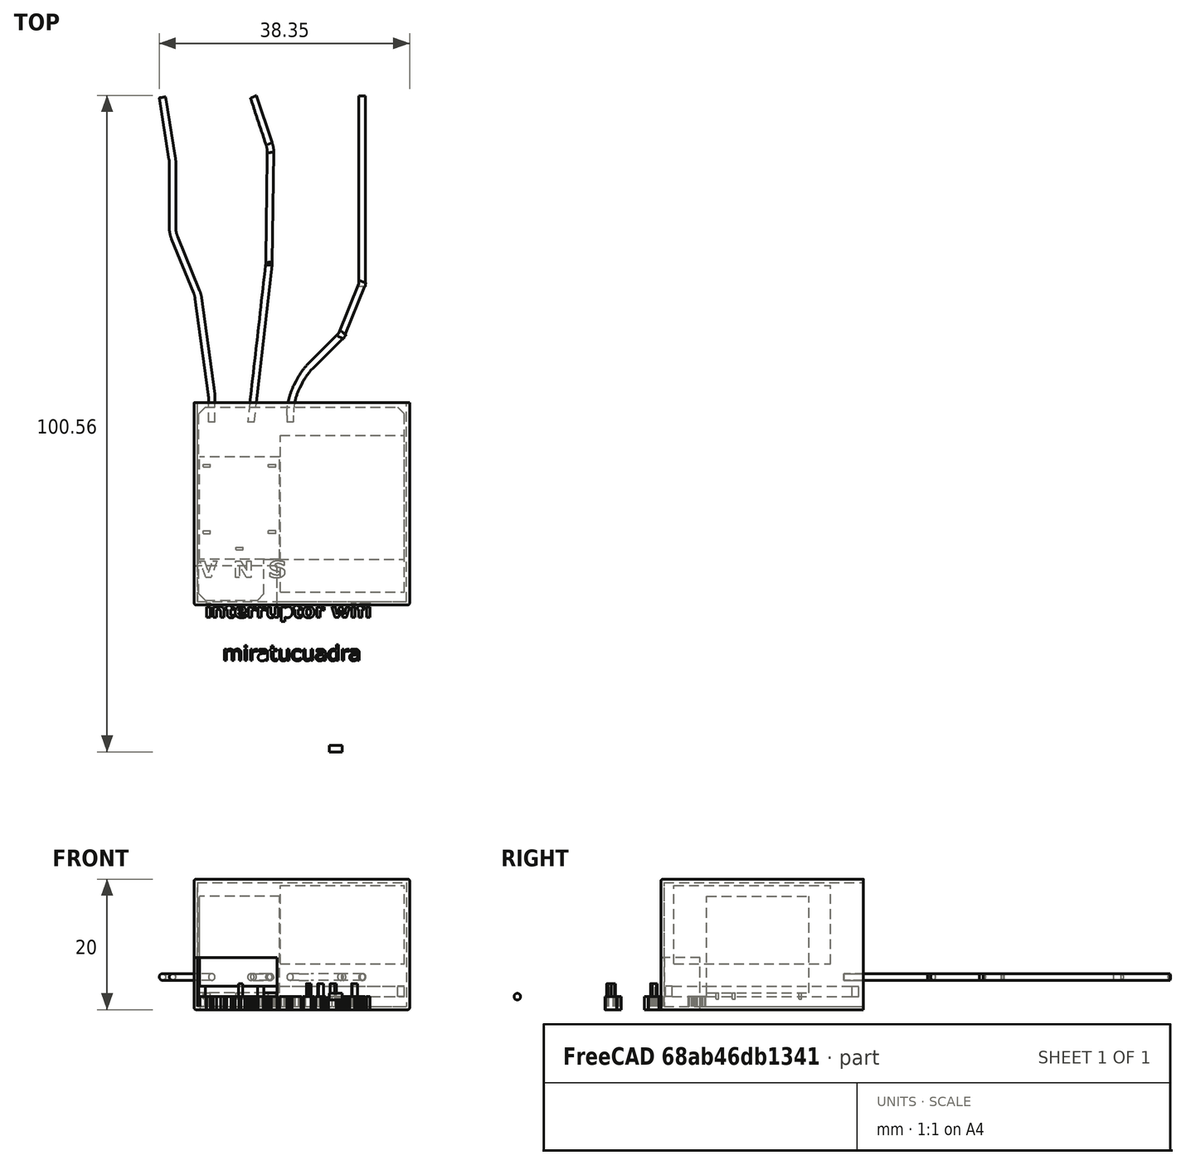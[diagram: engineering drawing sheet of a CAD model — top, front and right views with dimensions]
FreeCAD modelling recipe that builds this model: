
FCSTD DOCUMENT  (FreeCAD 0.20R29410 (Git))
Label: device01_funda_reprog
License: All rights reserved
LicenseURL: http://en.wikipedia.org/wiki/All_rights_reserved
objects: Part::Extrusion×42, Part::Feature×41, Part::Box×12, Part::Part2DObjectPython×6, Part::Cut×6, Part::MultiFuse×3, Part::Sweep×3, Part::Chamfer×2, Part::Fillet×1
note: 116 computed .brp shape members not serialized (recipe doc carries the construction recipe); baked Part::Feature solids carry a one-line shape summary decoded from their .brp

FEATURE [Part::Box] Box  label="fuente"
  AttacherType = Attacher::AttachEngine3D
  Height = 12
  Length = 19
  Placement = pos=(12.5,-5,5) rot=(0,0,1;0rad)
  Width = 24
FEATURE [Part::Box] Box002  label="placa"
  AttacherType = Attacher::AttachEngine3D
  Height = 1.6
  Length = 31.5
  Width = 23.3
FEATURE [Part::Box] Box003  label="placa2"
  AttacherType = Attacher::AttachEngine3D
  Height = 1.6
  Length = 10
  Placement = pos=(0,-6.3,0) rot=(0,0,1;0rad)
  Width = 6.3
FEATURE [Part::Chamfer] Chamfer
  Base = -> Box003
  Edges = 2 edges r=1: [Edge1,Edge5]
FEATURE [Part::Chamfer] Chamfer001
  Base = -> Box002
  Edges = 2 edges r=1: [Edge3,Edge7]
FEATURE [Part::MultiFuse] Fusion  label="plaqueta"
  Shapes = -> [Chamfer,Chamfer001]
FEATURE [Part::Box] Box004  label="cuerpo"
  AttacherType = Attacher::AttachEngine3D
  Height = 14.8
  Length = 15.7
  Placement = pos=(0,0,-1) rot=(0,0,1;0rad)
  Width = 12.3
FEATURE [Part::Box] Box005  label="pata002"
  AttacherType = Attacher::AttachEngine3D
  Height = 2.5
  Length = 0.4
  Placement = pos=(1.45,5.6,-2) rot=(0,0,1;0rad)
  Width = 1.1
FEATURE [Part::Box] Box006  label="pata003"
  AttacherType = Attacher::AttachEngine3D
  Height = 2.5
  Length = 0.4
  Placement = pos=(14.15,10.6,-2) rot=(0,0,1;0rad)
  Width = 1.1
FEATURE [Part::Box] Box007  label="pata004"
  AttacherType = Attacher::AttachEngine3D
  Height = 2.5
  Length = 0.4
  Placement = pos=(3.95,10.6,-2) rot=(0,0,1;0rad)
  Width = 1.1
FEATURE [Part::Box] Box008  label="pata005"
  AttacherType = Attacher::AttachEngine3D
  Height = 2.5
  Length = 0.4
  Placement = pos=(14.15,0.6,-2) rot=(0,0,1;0rad)
  Width = 1.1
FEATURE [Part::Box] Box009  label="pata1"
  AttacherType = Attacher::AttachEngine3D
  Height = 2.5
  Length = 0.4
  Placement = pos=(3.95,0.6,-2) rot=(0,0,1;0rad)
  Width = 1.1
FEATURE [Part::MultiFuse] Fusion001  label="relay"
  Placement = pos=(12.4,0,1.6) rot=(0,0,1;1.5708rad)
  Shapes = -> [Box009,Box007,Box005,Box006,Box008,Box004]
FEATURE [Part::Box] Box010  label="funda"
  AttacherType = Attacher::AttachEngine3D
  Height = 20
  Length = 33
  Placement = pos=(-0.7,-7,-2) rot=(0,0,1;0rad)
  Width = 31
FEATURE [Part::Part2DObjectPython] Circle  # Draft 2D object (typed FeaturePython)
  FirstAngle = 0
  LastAngle = 0
  MakeFace = true
  Placement = pos=(20,-17,0) rot=(0.57735,0.57735,0.57735;2.0944rad)
  Radius = 0.5
FEATURE [Part::Part2DObjectPython] DWire  # Draft 2D object (typed FeaturePython)
  ChamferSize = 0
  Closed = false
  End = (20,-11,0)
  FilletRadius = 4
  Length = 53.4054
  MakeFace = false
  Points = (6) [(-30,-1.83697e-15,0),(0,0,0),(10,-4,0),(16,-10,0),(18,-11,0),(20,-11,0)]
  Start = (-30,0,0)
  Subdivisions = 0
FEATURE [Part::Sweep] Sweep
  Frenet = false
  Sections = -> [Circle]
  Solid = true
  Spine = -> DWire
  Transition = 1
FEATURE [Part::Part2DObjectPython] DWire001  # Draft 2D object (typed FeaturePython)
  ChamferSize = 0
  Closed = false
  End = (-29.8507,-19.6083,0)
  FilletRadius = 4
  Length = 50.4185
  MakeFace = false
  Points = (4) [(20,-20,0),(-4.30719,-17.2304,0),(-22,-17,0),(-29.8507,-19.6083,0)]
  Start = (20,-20,0)
  Subdivisions = 0
FEATURE [Part::Part2DObjectPython] Circle001  # Draft 2D object (typed FeaturePython)
  FirstAngle = 0
  LastAngle = 0
  MakeFace = true
  Placement = pos=(20,-20,0) rot=(0.57735,0.57735,0.57735;2.0944rad)
  Radius = 0.5
FEATURE [Part::Sweep] Sweep001
  Frenet = false
  Placement = pos=(0,-3,0) rot=(0,0,1;0rad)
  Sections = -> [Circle001]
  Solid = true
  Spine = -> DWire001
  Transition = 1
FEATURE [Part::Part2DObjectPython] DWire002  # Draft 2D object (typed FeaturePython)
  ChamferSize = 0
  Closed = false
  End = (-29.774,-36.5606,0)
  FilletRadius = 4
  Length = 50.7764
  MakeFace = false
  Points = (6) [(20,-29,0),(16,-29,0),(0.525362,-31.1144,0),(-9,-35,0),(-20,-35,0),(-29.774,-36.5606,0)]
  Start = (20,-29,0)
  Subdivisions = 0
FEATURE [Part::Part2DObjectPython] Circle002  # Draft 2D object (typed FeaturePython)
  FirstAngle = 0
  LastAngle = 0
  MakeFace = true
  Placement = pos=(20,-29,0) rot=(0.57735,0.57735,0.57735;2.0944rad)
  Radius = 0.5
FEATURE [Part::Sweep] Sweep002
  Frenet = false
  Sections = -> [Circle002]
  Solid = true
  Spine = -> DWire002
  Transition = 1
FEATURE [Part::MultiFuse] Fusion002  label="cables"
  Placement = pos=(31,41,3) rot=(0,0,-1;1.5708rad)
  Shapes = -> [Sweep,Sweep001,Sweep002]
FEATURE [Part::Box] Box011  label="Cubo"
  AttacherType = Attacher::AttachEngine3D
  Height = 19
  Length = 32
  Placement = pos=(-0.2,-6.5,-1.5) rot=(0,0,1;0rad)
  Width = 35
FEATURE [Part::Cut] Cut  label="carcasa"
  Base = -> Box010
  Tool = -> Box011
FEATURE [Part::Fillet] Fillet  label="gabinete"
  Base = -> Cut
  Edges = 8 edges r=0.3: [Edge1,Edge2,Edge4,Edge5,Edge6,Edge7,Edge9,Edge16]
FEATURE [Part::Box] Box012  label="Cubo001"
  AttacherType = Attacher::AttachEngine3D
  Height = 10
  Length = 14
  Placement = pos=(-2,-11,-4) rot=(0,0,1;0rad)
  Width = 10
FEATURE [Part::Cut] Cut001
  Base = -> Fillet
  Tool = -> Box012
FEATURE [Part::Feature] path319
  shape: bbox 2.527 x 1.78 x 2e-07 mm, 0 faces, 0 solids (baked)
FEATURE [Part::Feature] path321
  shape: bbox 0.3287 x 0.3023 x 2e-07 mm, 0 faces, 0 solids (baked)
FEATURE [Part::Feature] path321001
  shape: bbox 0.2915 x 1.732 x 2e-07 mm, 0 faces, 0 solids (baked)
FEATURE [Part::Feature] path323
  shape: bbox 1.081 x 1.732 x 2e-07 mm, 0 faces, 0 solids (baked)
FEATURE [Part::Feature] path325
  shape: bbox 1.471 x 1.822 x 2e-07 mm, 0 faces, 0 solids (baked)
FEATURE [Part::Feature] path325001
  shape: bbox 0.8806 x 0.6852 x 2e-07 mm, 0 faces, 0 solids (baked)
FEATURE [Part::Feature] path327
  shape: bbox 1.09 x 2.263 x 2e-07 mm, 0 faces, 0 solids (baked)
FEATURE [Part::Feature] path329
  shape: bbox 1.448 x 1.78 x 2e-07 mm, 0 faces, 0 solids (baked)
FEATURE [Part::Feature] path331
  shape: bbox 1.405 x 1.811 x 2e-07 mm, 0 faces, 0 solids (baked)
FEATURE [Part::Feature] path333
  shape: bbox 1.448 x 1.78 x 2e-07 mm, 0 faces, 0 solids (baked)
FEATURE [Part::Feature] path335
  shape: bbox 1.471 x 1.822 x 2e-07 mm, 0 faces, 0 solids (baked)
FEATURE [Part::Feature] path335001
  shape: bbox 0.8806 x 0.6852 x 2e-07 mm, 0 faces, 0 solids (baked)
FEATURE [Part::Feature] path337
  shape: bbox 1.524 x 2.46 x 2e-07 mm, 0 faces, 0 solids (baked)
FEATURE [Part::Feature] path337001
  shape: bbox 0.9317 x 1.284 x 2e-07 mm, 0 faces, 0 solids (baked)
FEATURE [Part::Feature] path339
  shape: bbox 1.081 x 1.732 x 2e-07 mm, 0 faces, 0 solids (baked)
FEATURE [Part::Feature] path341
  shape: bbox 1.471 x 1.822 x 2e-07 mm, 0 faces, 0 solids (baked)
FEATURE [Part::Feature] path341001
  shape: bbox 0.8806 x 0.6852 x 2e-07 mm, 0 faces, 0 solids (baked)
FEATURE [Part::Feature] path357
  shape: bbox 2.643 x 2.596 x 2e-07 mm, 0 faces, 0 solids (baked)
FEATURE [Part::Feature] path354
  shape: bbox 2.361 x 2.596 x 2e-07 mm, 0 faces, 0 solids (baked)
FEATURE [Part::Feature] path351
  shape: bbox 2.22 x 2.69 x 2e-07 mm, 0 faces, 0 solids (baked)
FEATURE [Part::Feature] path288
  shape: bbox 0.5176 x 1.615 x 2e-07 mm, 0 faces, 0 solids (baked)
FEATURE [Part::Feature] path288001
  shape: bbox 0.5464 x 0.3925 x 2e-07 mm, 0 faces, 0 solids (baked)
FEATURE [Part::Feature] path290
  shape: bbox 1.622 x 1.659 x 2e-07 mm, 0 faces, 0 solids (baked)
FEATURE [Part::Feature] path292
  shape: bbox 1.215 x 2.108 x 2e-07 mm, 0 faces, 0 solids (baked)
FEATURE [Part::Feature] path294
  shape: bbox 1.708 x 1.708 x 2e-07 mm, 0 faces, 0 solids (baked)
FEATURE [Part::Feature] path294001
  shape: bbox 0.6715 x 0.3264 x 2e-07 mm, 0 faces, 0 solids (baked)
FEATURE [Part::Feature] path296
  shape: bbox 1.17 x 1.62 x 2e-07 mm, 0 faces, 0 solids (baked)
FEATURE [Part::Feature] path298
  shape: bbox 1.17 x 1.62 x 2e-07 mm, 0 faces, 0 solids (baked)
FEATURE [Part::Feature] path300
  shape: bbox 1.622 x 1.659 x 2e-07 mm, 0 faces, 0 solids (baked)
FEATURE [Part::Feature] path302
  shape: bbox 1.685 x 2.252 x 2e-07 mm, 0 faces, 0 solids (baked)
FEATURE [Part::Feature] path302001
  shape: bbox 0.6341 x 0.9303 x 2e-07 mm, 0 faces, 0 solids (baked)
FEATURE [Part::Feature] path304
  shape: bbox 1.215 x 2.108 x 2e-07 mm, 0 faces, 0 solids (baked)
FEATURE [Part::Feature] path306
  shape: bbox 1.769 x 1.715 x 2e-07 mm, 0 faces, 0 solids (baked)
FEATURE [Part::Feature] path306001
  shape: bbox 0.6959 x 0.9936 x 2e-07 mm, 0 faces, 0 solids (baked)
FEATURE [Part::Feature] path308
  shape: bbox 1.17 x 1.62 x 2e-07 mm, 0 faces, 0 solids (baked)
FEATURE [Part::Feature] path310
  shape: bbox 2.755 x 1.615 x 2e-07 mm, 0 faces, 0 solids (baked)
FEATURE [Part::Feature] path312
  shape: bbox 0.5176 x 1.615 x 2e-07 mm, 0 faces, 0 solids (baked)
FEATURE [Part::Feature] path312001
  shape: bbox 0.5464 x 0.3925 x 2e-07 mm, 0 faces, 0 solids (baked)
FEATURE [Part::Feature] path314
  shape: bbox 1.229 x 2.252 x 2e-07 mm, 0 faces, 0 solids (baked)
FEATURE [Part::Feature] path316
  shape: bbox 0.5176 x 1.615 x 2e-07 mm, 0 faces, 0 solids (baked)
FEATURE [Part::Feature] path316001
  shape: bbox 0.5464 x 0.3925 x 2e-07 mm, 0 faces, 0 solids (baked)
FEATURE [Part::Extrusion] Extrude005
  Base = -> Circle002
  Dir = (1,0,0)
  DirMode = 2
  FaceMakerClass = Part::FaceMakerBullseye
  LengthFwd = 2
  LengthRev = 0
  Solid = true
  Symmetric = false
FEATURE [Part::Extrusion] Extrude006
  Base = -> path319
  Dir = (0,0,-1)
  DirMode = 2
  FaceMakerClass = Part::FaceMakerBullseye
  LengthFwd = 2
  LengthRev = 0
  Solid = true
  Symmetric = false
FEATURE [Part::Extrusion] Extrude007
  Base = -> path321
  Dir = (0,0,-1)
  DirMode = 2
  FaceMakerClass = Part::FaceMakerBullseye
  LengthFwd = 2
  LengthRev = 0
  Solid = true
  Symmetric = false
FEATURE [Part::Extrusion] Extrude008
  Base = -> path321001
  Dir = (0,0,-1)
  DirMode = 2
  FaceMakerClass = Part::FaceMakerBullseye
  LengthFwd = 2
  LengthRev = 0
  Solid = true
  Symmetric = false
FEATURE [Part::Extrusion] Extrude009
  Base = -> path323
  Dir = (0,0,-1)
  DirMode = 2
  FaceMakerClass = Part::FaceMakerBullseye
  LengthFwd = 2
  LengthRev = 0
  Solid = true
  Symmetric = false
FEATURE [Part::Extrusion] Extrude010
  Base = -> path325
  Dir = (0,0,-1)
  DirMode = 2
  FaceMakerClass = Part::FaceMakerBullseye
  LengthFwd = 2
  LengthRev = 0
  Solid = true
  Symmetric = false
FEATURE [Part::Extrusion] Extrude011
  Base = -> path325001
  Dir = (0,0,1)
  DirMode = 2
  FaceMakerClass = Part::FaceMakerBullseye
  LengthFwd = 2
  LengthRev = 0
  Solid = true
  Symmetric = false
FEATURE [Part::Extrusion] Extrude012
  Base = -> path327
  Dir = (0,0,-1)
  DirMode = 2
  FaceMakerClass = Part::FaceMakerBullseye
  LengthFwd = 2
  LengthRev = 0
  Solid = true
  Symmetric = false
FEATURE [Part::Extrusion] Extrude013
  Base = -> path329
  Dir = (0,0,-1)
  DirMode = 2
  FaceMakerClass = Part::FaceMakerBullseye
  LengthFwd = 2
  LengthRev = 0
  Solid = true
  Symmetric = false
FEATURE [Part::Extrusion] Extrude014
  Base = -> path331
  Dir = (0,0,-1)
  DirMode = 2
  FaceMakerClass = Part::FaceMakerBullseye
  LengthFwd = 2
  LengthRev = 0
  Solid = true
  Symmetric = false
FEATURE [Part::Extrusion] Extrude015
  Base = -> path333
  Dir = (0,0,-1)
  DirMode = 2
  FaceMakerClass = Part::FaceMakerBullseye
  LengthFwd = 2
  LengthRev = 0
  Solid = true
  Symmetric = false
FEATURE [Part::Extrusion] Extrude016
  Base = -> path335
  Dir = (0,0,-1)
  DirMode = 2
  FaceMakerClass = Part::FaceMakerBullseye
  LengthFwd = 2
  LengthRev = 0
  Solid = true
  Symmetric = false
FEATURE [Part::Extrusion] Extrude017
  Base = -> path335001
  Dir = (0,0,1)
  DirMode = 2
  FaceMakerClass = Part::FaceMakerBullseye
  LengthFwd = 2
  LengthRev = 0
  Solid = true
  Symmetric = false
FEATURE [Part::Extrusion] Extrude018
  Base = -> path337
  Dir = (0,0,-1)
  DirMode = 2
  FaceMakerClass = Part::FaceMakerBullseye
  LengthFwd = 2
  LengthRev = 0
  Solid = true
  Symmetric = false
FEATURE [Part::Extrusion] Extrude019
  Base = -> path337001
  Dir = (0,0,1)
  DirMode = 2
  FaceMakerClass = Part::FaceMakerBullseye
  LengthFwd = 2
  LengthRev = 0
  Solid = true
  Symmetric = false
FEATURE [Part::Extrusion] Extrude020
  Base = -> path339
  Dir = (0,0,-1)
  DirMode = 2
  FaceMakerClass = Part::FaceMakerBullseye
  LengthFwd = 2
  LengthRev = 0
  Solid = true
  Symmetric = false
FEATURE [Part::Extrusion] Extrude021
  Base = -> path341
  Dir = (0,0,-1)
  DirMode = 2
  FaceMakerClass = Part::FaceMakerBullseye
  LengthFwd = 2
  LengthRev = 0
  Solid = true
  Symmetric = false
FEATURE [Part::Extrusion] Extrude022
  Base = -> path341001
  Dir = (0,0,1)
  DirMode = 2
  FaceMakerClass = Part::FaceMakerBullseye
  LengthFwd = 2
  LengthRev = 0
  Solid = true
  Symmetric = false
FEATURE [Part::Extrusion] Extrude023
  Base = -> path357
  Dir = (0,0,-1)
  DirMode = 2
  FaceMakerClass = Part::FaceMakerBullseye
  LengthFwd = 2
  LengthRev = 0
  Solid = true
  Symmetric = false
FEATURE [Part::Extrusion] Extrude024
  Base = -> path354
  Dir = (0,0,-1)
  DirMode = 2
  FaceMakerClass = Part::FaceMakerBullseye
  LengthFwd = 2
  LengthRev = 0
  Solid = true
  Symmetric = false
FEATURE [Part::Extrusion] Extrude025
  Base = -> path351
  Dir = (0,0,-1)
  DirMode = 2
  FaceMakerClass = Part::FaceMakerBullseye
  LengthFwd = 2
  LengthRev = 0
  Solid = true
  Symmetric = false
FEATURE [Part::Extrusion] Extrude026
  Base = -> path288
  Dir = (0,0,-1)
  DirMode = 2
  FaceMakerClass = Part::FaceMakerBullseye
  LengthFwd = 2
  LengthRev = 0
  Solid = true
  Symmetric = false
FEATURE [Part::Extrusion] Extrude027
  Base = -> path288001
  Dir = (0,0,-1)
  DirMode = 2
  FaceMakerClass = Part::FaceMakerBullseye
  LengthFwd = 2
  LengthRev = 0
  Solid = true
  Symmetric = false
FEATURE [Part::Extrusion] Extrude028
  Base = -> path290
  Dir = (0,0,-1)
  DirMode = 2
  FaceMakerClass = Part::FaceMakerBullseye
  LengthFwd = 2
  LengthRev = 0
  Solid = true
  Symmetric = false
FEATURE [Part::Extrusion] Extrude029
  Base = -> path292
  Dir = (0,0,-1)
  DirMode = 2
  FaceMakerClass = Part::FaceMakerBullseye
  LengthFwd = 2
  LengthRev = 0
  Solid = true
  Symmetric = false
FEATURE [Part::Extrusion] Extrude030
  Base = -> path294
  Dir = (0,0,-1)
  DirMode = 2
  FaceMakerClass = Part::FaceMakerBullseye
  LengthFwd = 2
  LengthRev = 0
  Solid = true
  Symmetric = false
FEATURE [Part::Extrusion] Extrude032
  Base = -> path296
  Dir = (0,0,-1)
  DirMode = 2
  FaceMakerClass = Part::FaceMakerBullseye
  LengthFwd = 2
  LengthRev = 0
  Solid = true
  Symmetric = false
FEATURE [Part::Extrusion] Extrude033
  Base = -> path298
  Dir = (0,0,-1)
  DirMode = 2
  FaceMakerClass = Part::FaceMakerBullseye
  LengthFwd = 2
  LengthRev = 0
  Solid = true
  Symmetric = false
FEATURE [Part::Extrusion] Extrude034
  Base = -> path300
  Dir = (0,0,-1)
  DirMode = 2
  FaceMakerClass = Part::FaceMakerBullseye
  LengthFwd = 2
  LengthRev = 0
  Solid = true
  Symmetric = false
FEATURE [Part::Extrusion] Extrude035
  Base = -> path302
  Dir = (0,0,-1)
  DirMode = 2
  FaceMakerClass = Part::FaceMakerBullseye
  LengthFwd = 2
  LengthRev = 0
  Solid = true
  Symmetric = false
FEATURE [Part::Extrusion] Extrude037
  Base = -> path304
  Dir = (0,0,-1)
  DirMode = 2
  FaceMakerClass = Part::FaceMakerBullseye
  LengthFwd = 2
  LengthRev = 0
  Solid = true
  Symmetric = false
FEATURE [Part::Extrusion] Extrude038
  Base = -> path306
  Dir = (0,0,-1)
  DirMode = 2
  FaceMakerClass = Part::FaceMakerBullseye
  LengthFwd = 2
  LengthRev = 0
  Solid = true
  Symmetric = false
FEATURE [Part::Extrusion] Extrude039
  Base = -> path306001
  Dir = (0,0,1)
  DirMode = 2
  FaceMakerClass = Part::FaceMakerBullseye
  LengthFwd = 2
  LengthRev = 0
  Solid = true
  Symmetric = false
FEATURE [Part::Extrusion] Extrude040
  Base = -> path308
  Dir = (0,0,-1)
  DirMode = 2
  FaceMakerClass = Part::FaceMakerBullseye
  LengthFwd = 2
  LengthRev = 0
  Solid = true
  Symmetric = false
FEATURE [Part::Extrusion] Extrude041
  Base = -> path310
  Dir = (0,0,-1)
  DirMode = 2
  FaceMakerClass = Part::FaceMakerBullseye
  LengthFwd = 2
  LengthRev = 0
  Solid = true
  Symmetric = false
FEATURE [Part::Extrusion] Extrude042
  Base = -> path312
  Dir = (0,0,-1)
  DirMode = 2
  FaceMakerClass = Part::FaceMakerBullseye
  LengthFwd = 2
  LengthRev = 0
  Solid = true
  Symmetric = false
FEATURE [Part::Extrusion] Extrude043
  Base = -> path312001
  Dir = (0,0,-1)
  DirMode = 2
  FaceMakerClass = Part::FaceMakerBullseye
  LengthFwd = 2
  LengthRev = 0
  Solid = true
  Symmetric = false
FEATURE [Part::Extrusion] Extrude044
  Base = -> path314
  Dir = (0,0,-1)
  DirMode = 2
  FaceMakerClass = Part::FaceMakerBullseye
  LengthFwd = 2
  LengthRev = 0
  Solid = true
  Symmetric = false
FEATURE [Part::Extrusion] Extrude045
  Base = -> path316
  Dir = (0,0,-1)
  DirMode = 2
  FaceMakerClass = Part::FaceMakerBullseye
  LengthFwd = 2
  LengthRev = 0
  Solid = true
  Symmetric = false
FEATURE [Part::Extrusion] Extrude046
  Base = -> path316001
  Dir = (0,0,-1)
  DirMode = 2
  FaceMakerClass = Part::FaceMakerBullseye
  LengthFwd = 2
  LengthRev = 0
  Solid = true
  Symmetric = false
FEATURE [Part::Cut] Cut002
  Base = -> Extrude010
  Tool = -> Extrude011
FEATURE [Part::Extrusion] Extrude031
  Base = -> path294001
  Dir = (0,0,1)
  DirMode = 2
  FaceMakerClass = Part::FaceMakerBullseye
  LengthFwd = 2
  LengthRev = 0
  Solid = true
  Symmetric = false
FEATURE [Part::Extrusion] Extrude036
  Base = -> path302001
  Dir = (0,0,1)
  DirMode = 2
  FaceMakerClass = Part::FaceMakerBullseye
  LengthFwd = 2
  LengthRev = 0
  Solid = true
  Symmetric = false
FEATURE [Part::Cut] Cut004
  Base = -> Extrude035
  Tool = -> Extrude036
FEATURE [Part::Cut] Cut005
  Base = -> Extrude035
  Tool = -> Extrude036
FEATURE [Part::Cut] Cut006
  Base = -> Extrude035
  Tool = -> Extrude036
